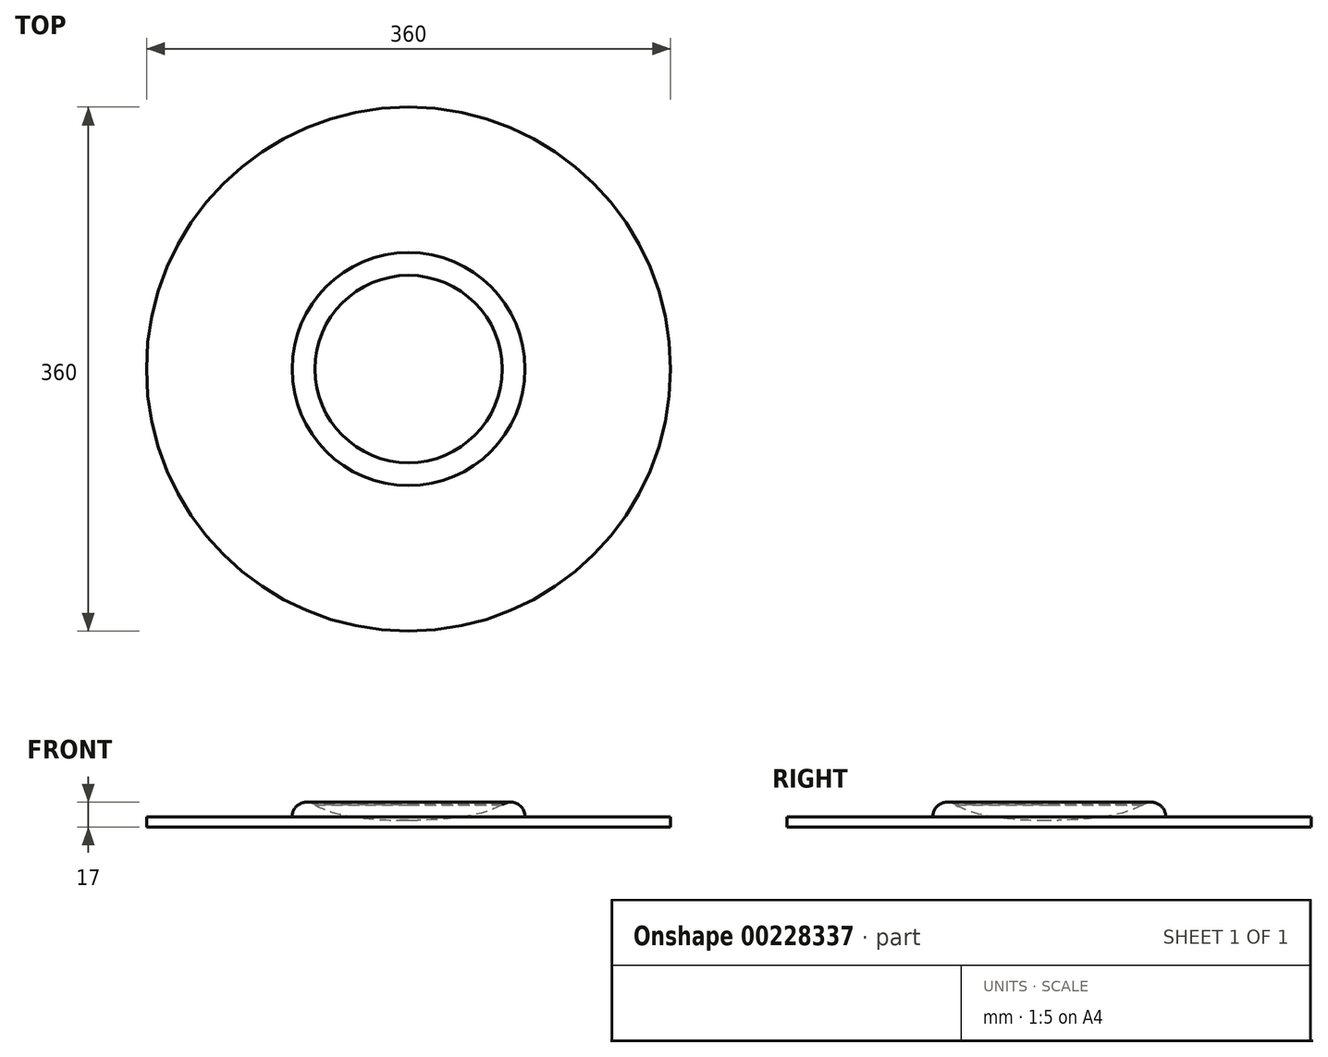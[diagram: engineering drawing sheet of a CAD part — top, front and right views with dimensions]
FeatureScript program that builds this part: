
annotation { "Feature Type Name" : "Feature", "Feature Type Description" : "" }
export const myFeature = defineFeature(function(context is Context, id is Id, definition is map)
    precondition{}
    {
        {
            var Q0;
            Q0=qCreatedBy(makeId("Right.planeOp"),FACE);
            var sketch = newSketch(context, id + "F0", { "sketchPlane" : qUnion([Q0])});
            skLineSegment(sketch, "E0.right", {"start": v(-180, 0) * mm, "end": v(-180, 7) * mm});
            skLineSegment(sketch, "E1.trimOffspring", {"start": v(-80, 7) * mm, "end": v(-180, 7) * mm});
            skLineSegment(sketch, "E2.trimOffspring", {"start": v(-80, 13.28) * mm, "end": v(-80, 13.28) * mm});
            skPoint(sketch, "E3.visualSharp", {"position": v(-80, 13.28) * mm});
            skArc(sketch, "E3.filletArc", {"start": v(-64.33, 15.24) * mm, "mid": v(-74.66, 15.85) * mm, "end": v(-80, 7) * mm});
            skLineSegment(sketch, "E4", {"start": v(0, 4.7) * mm, "end": v(0, 0) * mm});
            skLineSegment(sketch, "E5", {"start": v(-180, 0) * mm, "end": v(0, 0) * mm});
            skFitSpline(sketch, "E6", {"points": [v(-64.33, 15.24) * mm, v(-55.88, 11.3) * mm, v(-36, 6.74) * mm, v(-10.66, 4.68) * mm, v(0, 4.7) * mm], "startDerivative": vector(39.34, -21) * mm, "endDerivative": vector(45.68, 1.05) * mm});
            skLineSegment(sketch, "E7", {"start": v(0, 20.4) * mm, "end": v(0, -17.67) * mm, "construction": true});
            skSolve(sketch);
        }
        {
            var Q0;
            Q0 = qSketchRegion(id + "F0", true);
            var Q1;
            Q1=sQuery(id+"F0.wireOp",EDGE,"E7");
            revolve(context, id + "F1", {"entities" : qUnion([Q0]), "axis" : qUnion([Q1]), "revolveType" : RevolveType.FULL});
        }
    });
